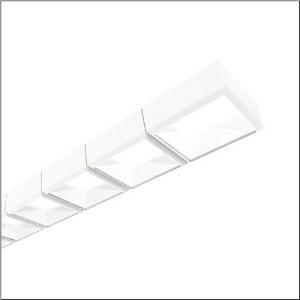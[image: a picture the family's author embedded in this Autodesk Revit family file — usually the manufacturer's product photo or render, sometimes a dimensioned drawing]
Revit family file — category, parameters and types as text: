
# Revit family: scriptus_r__11_5mz313d0twb_9c96
name_source: partatom
category: Lighting Fixtures
units: mm (PartAtom-declared; Revit-internal decimal feet)

## family parameters
Cut with Voids When Loaded = No
Host = Face
Light Source = No
Part Type = Normal
Room Calculation Point = No
Round Connector Dimension = Use Diameter
Shared = No

## types (1)
- --- (1 x LED 3000K+6500K / CRI = 80 (unbekannt), 3390 lm / 3550 lm, 3000K)
    Apparent Load = 107 VA
    CIE Flux Codes = 0 0 0 0 100 / 82 95 99 100 100
    Color Rendering = 80
    Color Temperature = 3000K
    Default Elevation = 1800 mm
    Description = Scriptus® 11, office luminaire, primary optical cover: lenses, CAT 2 (L<= 3000cd/m²), light emission: direct/indirect distribution, primary light characteristic: symmetric, installation type: suspended mounting, LED rated luminous flux: 13.880 lm, light colour: 8tw, colour temperature: 3000..6500K, control gear: ECG DALI, with terminal, 5-pole, mains connection: 230V, AC, 50Hz, rated input power: 110W, LED control gear: ECG DALI, housing, luminaire housing, of aluminium, traffic white (RAL 9016), length: 2.648 mm, width: 114 mm, height: 57mm, protection rating (complete): IP20, insulation class (complete): insulation class I (protective earthing), certification: CE, protection symbol: F, permissible ambient temperature for indoor applications: <= +25°C, standard: EN 50419, packaging unit: 1 piece
    Height = 57 mm
    Lamp = 1 x LED 3000K+6500K / CRI >= 80 (unbekannt)
    Lamp Light Flux = 3390 lm / 3550 lm
    Lamp count = 1
    Length = 2648 mm
    Luminous efficacy = 130 lm/W
    Manufacturer = Siteco
    ModVariant = No
    Model = 5MZ313D0TWB
    Mounting Place = Ceiling
    Mounting Type = Pendant
    Number of Poles = 1
    OnlyDefault = Yes
    Power Factor = 1
    Product Name = Scriptus® 11
    Product group = office luminaire | ceiling pendant
    ProductGroupID = 905
    Protection Class = Protection class I
    Protection Degree = IP 20
    RLX_Detail_Level = 1
    RlxData = <blob elided: 32021 chars, md5=cc036233>
    Socket = socket
    Standby Power = 0 W
    System Light Flux = 13880 lm
    System Power = 107 W
    Type Comments = individual setting: colour temperature 6500K
    Type Image = l_1004839.jpg
    URL = http://relux.com
    VarID = @adj_146258
    Voltage = 0 V
    Weight = 0.00 kg
    Width = 114 mm

## geometry (parser evidence)
native form markers: Blend x4, Sweep x17
no freeform markers — native parametric forms only
